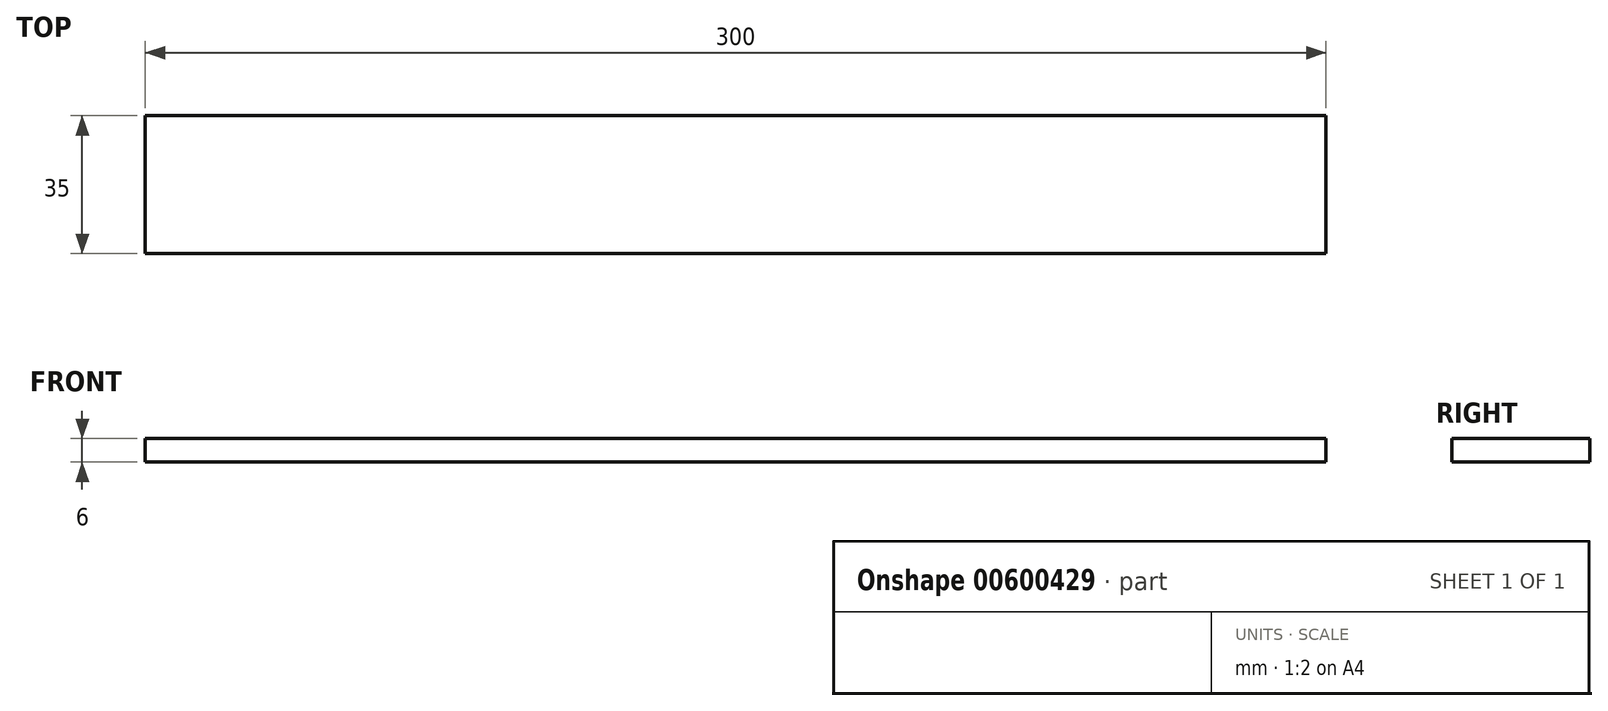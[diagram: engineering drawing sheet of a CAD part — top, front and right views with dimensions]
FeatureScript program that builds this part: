
annotation { "Feature Type Name" : "Feature", "Feature Type Description" : "" }
export const myFeature = defineFeature(function(context is Context, id is Id, definition is map)
    precondition{}
    {
        {
            var Q0;
            Q0=qCreatedBy(makeId("Top.planeOp"),FACE);
            var sketch = newSketch(context, id + "F0", { "sketchPlane" : qUnion([Q0])});
            skLineSegment(sketch, "E0.bottom", {"start": v(-237.11, -70.6) * mm, "end": v(62.89, -70.6) * mm});
            skLineSegment(sketch, "E0.top", {"start": v(-237.11, -105.6) * mm, "end": v(62.89, -105.6) * mm});
            skLineSegment(sketch, "E0.left", {"start": v(-237.11, -70.6) * mm, "end": v(-237.11, -105.6) * mm});
            skLineSegment(sketch, "E0.right", {"start": v(62.89, -70.6) * mm, "end": v(62.89, -105.6) * mm});
            skSolve(sketch);
        }
        {
            var Q0;
            Q0 = qSketchRegion(id + "F0", true);
            extrude(context, id + "F1", {"entities" : qUnion([Q0]), "depth" : 6 * mm, "offsetDistance" : 25 * mm});
        }
    });
